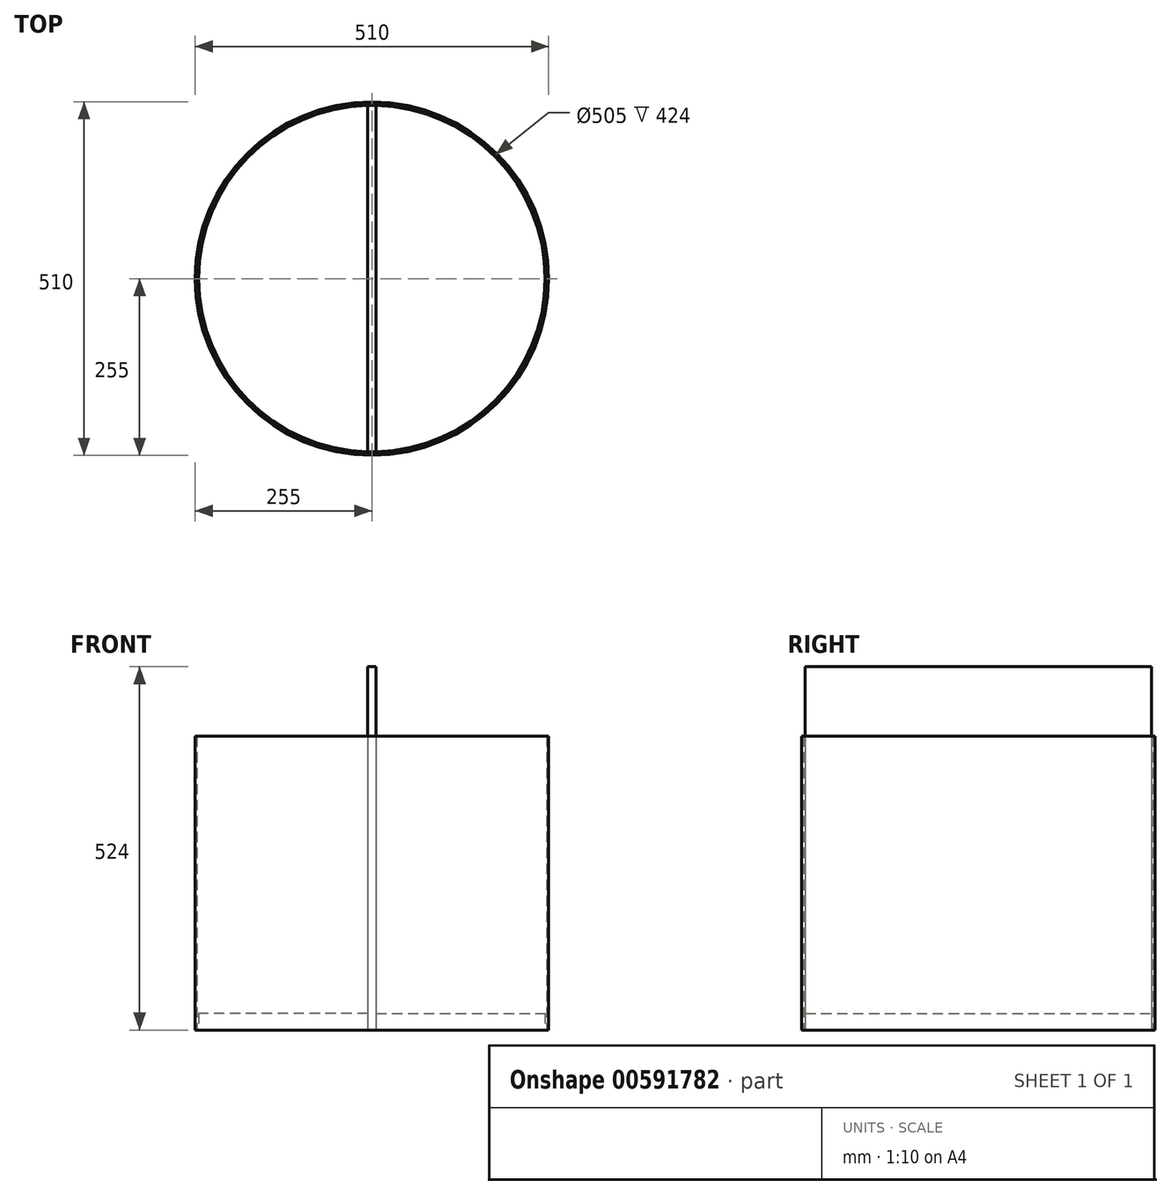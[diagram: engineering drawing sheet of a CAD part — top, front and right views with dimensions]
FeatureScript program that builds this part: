
annotation { "Feature Type Name" : "Feature", "Feature Type Description" : "" }
export const myFeature = defineFeature(function(context is Context, id is Id, definition is map)
    precondition{}
    {
        {
            var Q0;
            Q0=qCreatedBy(makeId("Top.planeOp"),FACE);
            var sketch = newSketch(context, id + "F0", { "sketchPlane" : qUnion([Q0])});
            skCircle(sketch, "E0", {"center": v(0, 0) * mm, "radius": 250 * mm});
            skSolve(sketch);
        }
        {
            var Q0;
            Q0=qSketchRegion(id+"F0",true);
            extrude(context, id + "F1", {"entities" : qUnion([Q0]), "depth" : 24 * mm});
        }
        {
            var Q0;
            Q0=qCreatedBy(makeId("Top.planeOp"),FACE);
            var sketch = newSketch(context, id + "F2", { "sketchPlane" : qUnion([Q0])});
            skLineSegment(sketch, "E1.bottom", {"start": v(6, 250) * mm, "end": v(-6, 250) * mm});
            skLineSegment(sketch, "E1.top", {"start": v(6, -250) * mm, "end": v(-6, -250) * mm});
            skLineSegment(sketch, "E1.left", {"start": v(6, 250) * mm, "end": v(6, -250) * mm});
            skLineSegment(sketch, "E1.right", {"start": v(-6, 250) * mm, "end": v(-6, -250) * mm});
            skPoint(sketch, "E1.middle", {"position": v(0, 0) * mm});
            skSolve(sketch);
        }
        {
            var Q0;
            Q0=qSketchRegion(id+"F2",true);
            extrude(context, id + "F3", {"entities" : qUnion([Q0]), "operationType" : NewBodyOperationType.ADD, "depth" : 524 * mm});
        }
        {
            var Q0;
            Q0=qCreatedBy(makeId("Top.planeOp"),FACE);
            var sketch = newSketch(context, id + "F4", { "sketchPlane" : qUnion([Q0])});
            skCircle(sketch, "E2", {"center": v(0, 0) * mm, "radius": 250 * mm});
            skCircle(sketch, "E3", {"center": v(0, 0) * mm, "radius": 252.5 * mm});
            skSolve(sketch);
        }
        {
            var Q0;
            Q0=sQuery(id+"F4.wireOp",EDGE,"E3");
            extrude(context, id + "F5", {"bodyType" : ToolBodyType.SURFACE, "surfaceEntities" : qUnion([Q0]), "depth" : 524 * mm});
        }
        {
            var Q0;
            Q0=qCreatedBy(makeId("Top.planeOp"),FACE);
            var sketch = newSketch(context, id + "F6", { "sketchPlane" : qUnion([Q0])});
            skCircle(sketch, "E4", {"center": v(0, 0) * mm, "radius": 252.5 * mm});
            skCircle(sketch, "E5", {"center": v(0, 0) * mm, "radius": 255 * mm});
            skSolve(sketch);
        }
        {
            var Q0;
            Q0=qSketchRegion(id+"F6",true);
            extrude(context, id + "F7", {"entities" : qUnion([Q0]), "depth" : 424 * mm});
        }
    });
